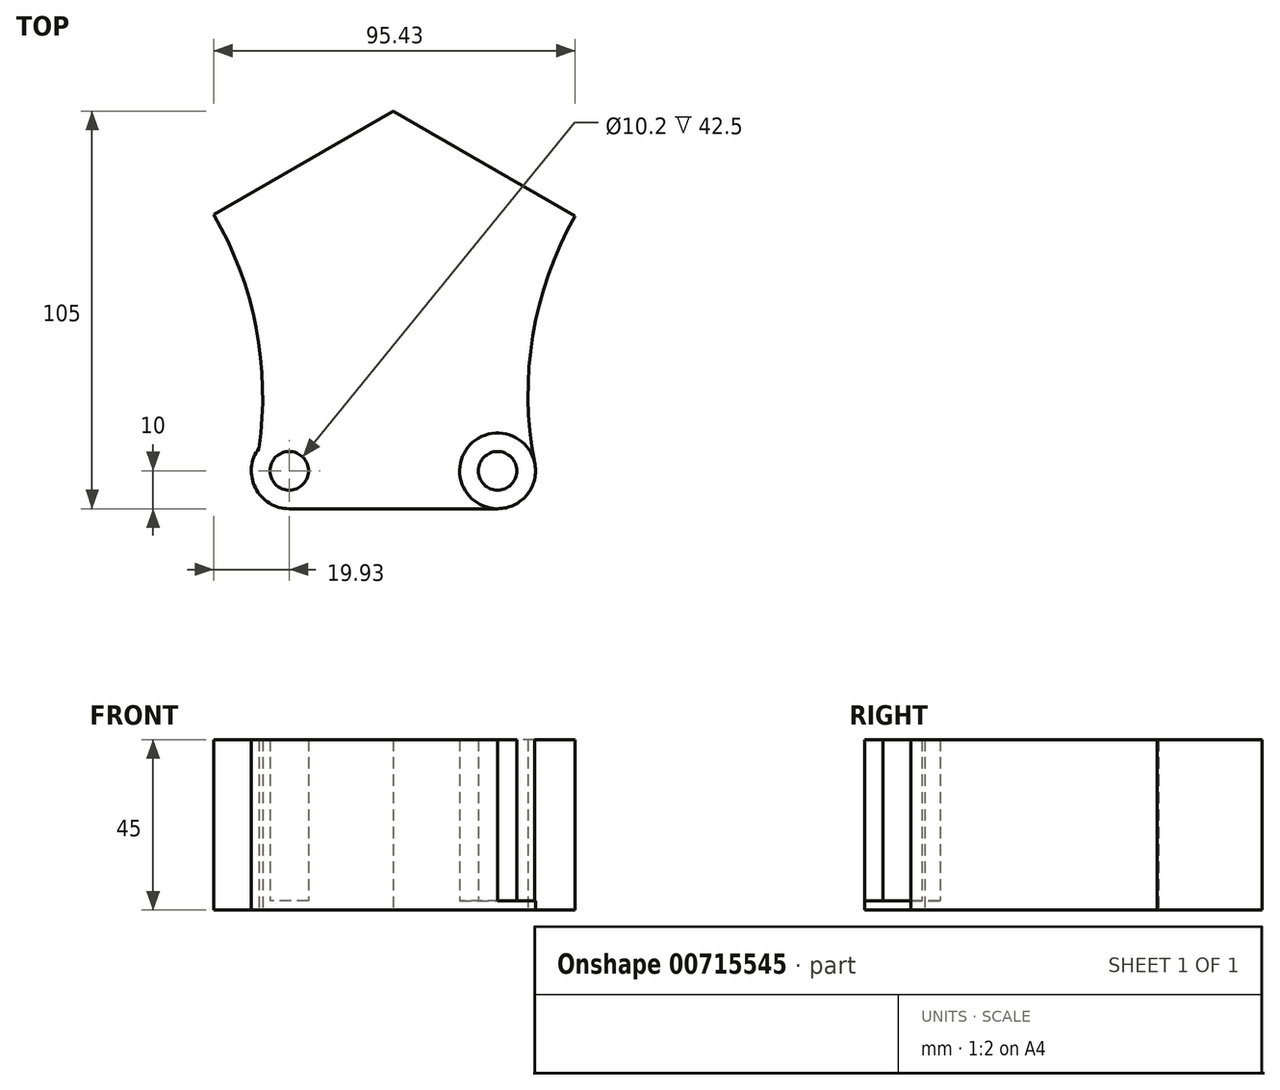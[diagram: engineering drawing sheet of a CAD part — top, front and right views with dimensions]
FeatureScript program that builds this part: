
annotation { "Feature Type Name" : "Feature", "Feature Type Description" : "" }
export const myFeature = defineFeature(function(context is Context, id is Id, definition is map)
    precondition{}
    {
        {
            var Q0;
            Q0=qCreatedBy(makeId("Top.planeOp"),FACE);
            var sketch = newSketch(context, id + "F0", { "sketchPlane" : qUnion([Q0])});
            skCircle(sketch, "E0", {"center": v(0, 0) * mm, "radius": 57.15 * mm, "construction": true});
            skLineSegment(sketch, "E1.bottom", {"start": v(110, 110) * mm, "end": v(-110, 110) * mm, "construction": true});
            skLineSegment(sketch, "E1.top", {"start": v(110, -110) * mm, "end": v(-110, -110) * mm, "construction": true});
            skLineSegment(sketch, "E1.left", {"start": v(110, 110) * mm, "end": v(110, -110) * mm, "construction": true});
            skLineSegment(sketch, "E1.right", {"start": v(-110, 110) * mm, "end": v(-110, -110) * mm, "construction": true});
            skLineSegment(sketch, "E2", {"start": v(0, 0) * mm, "end": v(0, -95) * mm});
            skLineSegment(sketch, "E3", {"start": v(0, 0) * mm, "end": v(-75.67, -43.69) * mm});
            skLineSegment(sketch, "E4", {"start": v(0, 0) * mm, "end": v(-70.96, 40.97) * mm});
            skLineSegment(sketch, "E5.MirrorCS", {"start": v(0, 0) * mm, "end": v(75.67, -43.69) * mm});
            skLineSegment(sketch, "E6.MirrorCS", {"start": v(0, 0) * mm, "end": v(70.96, 40.97) * mm});
            skCircle(sketch, "E7", {"center": v(-27.5, -95) * mm, "radius": 5.1 * mm});
            skCircle(sketch, "E8", {"center": v(-27.5, -95) * mm, "radius": 10 * mm});
            skCircle(sketch, "E9.MirrorC", {"center": v(27.5, -95) * mm, "radius": 5.1 * mm});
            skCircle(sketch, "E10.MirrorC", {"center": v(27.5, -95) * mm, "radius": 10 * mm});
            skLineSegment(sketch, "E11", {"start": v(-27.5, -95) * mm, "end": v(-27.5, -105) * mm});
            skLineSegment(sketch, "E12", {"start": v(-27.5, -105) * mm, "end": v(27.5, -105) * mm});
            skCircle(sketch, "E13.1.0", {"center": v(96.67, 23.49) * mm, "radius": 10 * mm});
            skCircle(sketch, "E13.1.1", {"center": v(96.67, 23.49) * mm, "radius": 5.1 * mm});
            skLineSegment(sketch, "E13.1.2", {"start": v(105.33, 28.49) * mm, "end": v(77.83, 76.12) * mm});
            skCircle(sketch, "E13.1.3", {"center": v(69.17, 71.12) * mm, "radius": 10 * mm});
            skCircle(sketch, "E13.1.4", {"center": v(69.17, 71.12) * mm, "radius": 5.1 * mm});
            skCircle(sketch, "E13.2.0", {"center": v(-68.03, 71.78) * mm, "radius": 10 * mm});
            skCircle(sketch, "E13.2.1", {"center": v(-68.03, 71.78) * mm, "radius": 5.1 * mm});
            skLineSegment(sketch, "E13.2.2", {"start": v(-76.69, 76.78) * mm, "end": v(-104.19, 29.15) * mm});
            skCircle(sketch, "E13.2.3", {"center": v(-95.53, 24.15) * mm, "radius": 10 * mm});
            skCircle(sketch, "E13.2.4", {"center": v(-95.53, 24.15) * mm, "radius": 5.1 * mm});
            skPoint(sketch, "E13.center", {"position": v(0.38, 0.09) * mm});
            skArc(sketch, "E14", {"start": v(95.53, 13.55) * mm, "mid": v(47.22, -29.11) * mm, "end": v(37.25, -92.79) * mm});
            skArc(sketch, "E15.1.0", {"start": v(-58.85, 75.76) * mm, "mid": v(2.25, 55.25) * mm, "end": v(62.38, 78.46) * mm});
            skArc(sketch, "E15.2.0", {"start": v(-35.53, -89.05) * mm, "mid": v(-48.32, -25.87) * mm, "end": v(-98.49, 14.6) * mm});
            skSolve(sketch);
        }
        {
            var Q0;
            {var subQ0=sQuery(id+"F0.wireOp",EDGE,"E12");Q0=makeQuery(id+"F0.imprint","IMPRINT",FACE,{"disambiguationData":[TD([[makeQuery(id+"F0.imprint","IMPRINT",EDGE,{"derivedFrom":subQ0}),1.0]])]});}
            var Q1;
            Q1=makeQuery(id+"F0.imprint","IMPRINT",FACE,{"disambiguationData":[TD([[makeQuery(id+"F0.imprint","IMPRINT",EDGE,{"derivedFrom":sQuery(id+"F0.wireOp",EDGE,"E7")}),-1.0]])]});
            var Q2;
            Q2=makeQuery(id+"F0.imprint","IMPRINT",FACE,{"disambiguationData":[TD([[makeQuery(id+"F0.imprint","IMPRINT",EDGE,{"derivedFrom":sQuery(id+"F0.wireOp",EDGE,"E9.MirrorC")}),1.0]])]});
            extrude(context, id + "F1", {"entities" : qUnion([Q0, Q1, Q2]), "depth" : 45 * mm, "offsetDistance" : 25 * mm});
        }
        {
            var Q0;
            Q0=makeQuery(id+"F0.imprint","IMPRINT",FACE,{"disambiguationData":[TD([[makeQuery(id+"F0.imprint","IMPRINT",EDGE,{"derivedFrom":sQuery(id+"F0.wireOp",EDGE,"E9.MirrorC")}),-1.0]])]});
            var Q1;
            Q1=makeQuery(id+"F0.imprint","IMPRINT",FACE,{"disambiguationData":[TD([[makeQuery(id+"F0.imprint","IMPRINT",EDGE,{"derivedFrom":sQuery(id+"F0.wireOp",EDGE,"E7")}),1.0]])]});
            extrude(context, id + "F2", {"entities" : qUnion([Q0, Q1]), "operationType" : NewBodyOperationType.ADD, "depth" : 2.5 * mm, "offsetDistance" : 25 * mm});
        }
        {
            var Q0;
            Q0=makeQuery(id+"F1.opExtrude","SWEPT_FACE",FACE,{"disambiguationData":[OSD([sQuery(id+"F0.wireOp",EDGE,"E12")])]});
            cPlane(context, id + "F3", {"entities" : qUnion([Q0]), "cplaneType" : CPlaneType.OFFSET, "offset" : 16.5 * mm, "oppositeDirection" : true, "width" : 150 * mm, "height" : 150 * mm});
        }
    });
